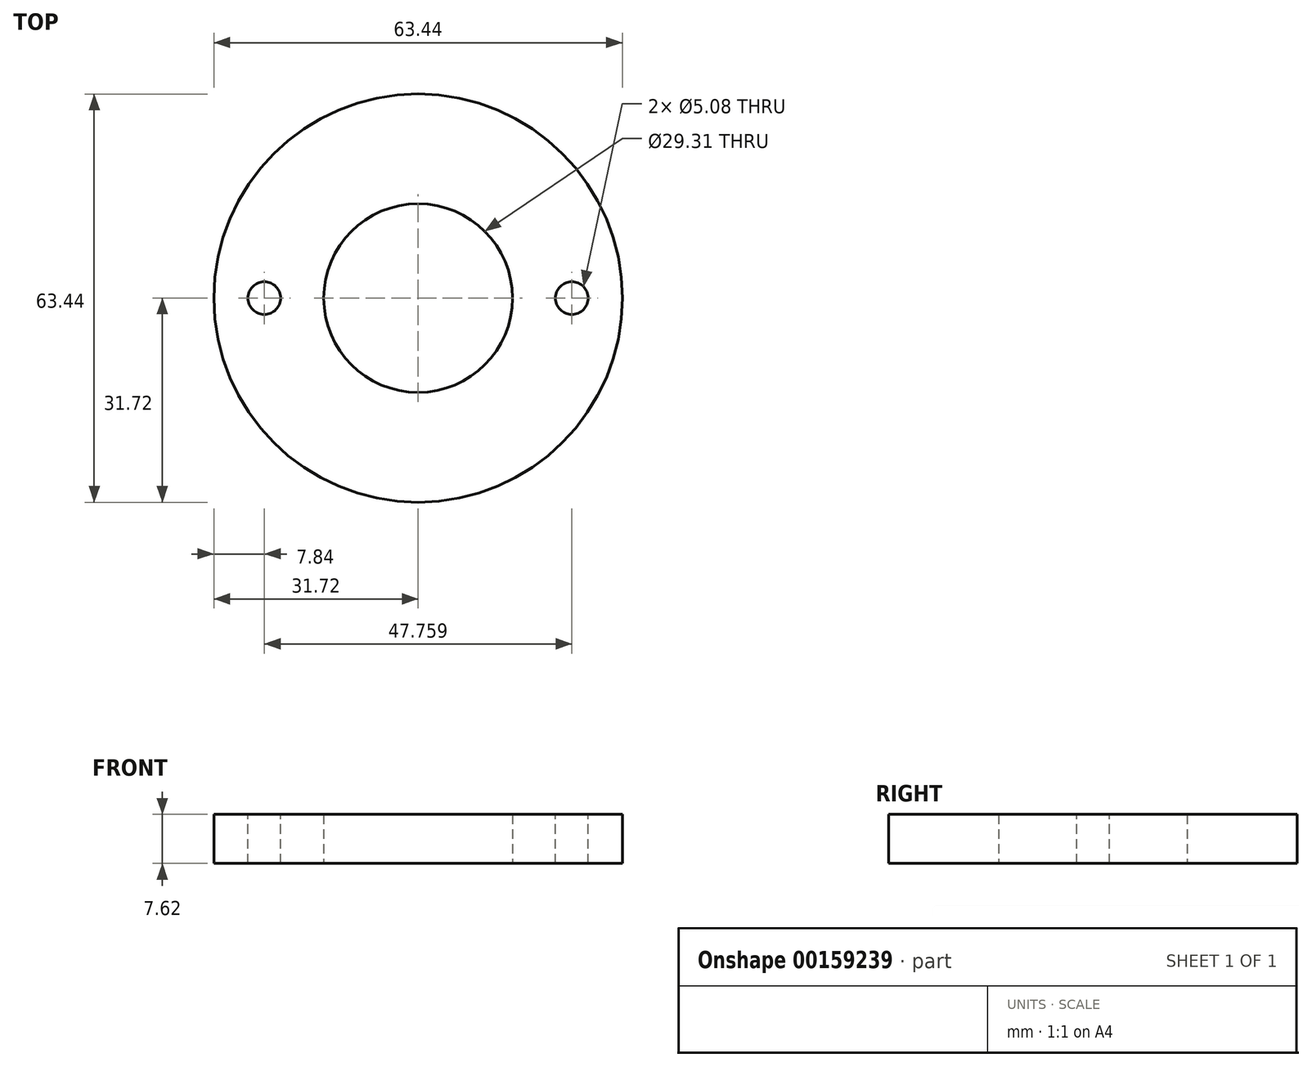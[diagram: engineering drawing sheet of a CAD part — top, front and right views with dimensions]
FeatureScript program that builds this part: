
annotation { "Feature Type Name" : "Feature", "Feature Type Description" : "" }
export const myFeature = defineFeature(function(context is Context, id is Id, definition is map)
    precondition{}
    {
        {
            var Q0;
            Q0=qCreatedBy(makeId("Top.planeOp"),FACE);
            var sketch = newSketch(context, id + "F0", { "sketchPlane" : qUnion([Q0])});
            skCircle(sketch, "E0", {"center": v(0, 0) * mm, "radius": 31.72 * mm});
            skCircle(sketch, "E1", {"center": v(0, 0) * mm, "radius": 14.66 * mm});
            skSolve(sketch);
        }
        {
            var Q0;
            Q0=makeQuery(id+"F0.imprint","IMPRINT",FACE,{"disambiguationData":[TD([[makeQuery(id+"F0.imprint","IMPRINT",EDGE,{"derivedFrom":sQuery(id+"F0.wireOp",EDGE,"E0")}),1.0]])]});
            extrude(context, id + "F1", {"entities" : qUnion([Q0]), "depth" : 7.62 * mm});
        }
        {
            var Q0;
            Q0=makeQuery(id+"F1.opExtrude","CAP_FACE",FACE,{"disambiguationData":[OSD([sQuery(id+"F0.wireOp",EDGE,"E0"),sQuery(id+"F0.wireOp",EDGE,"E1")])],"isStart":false});
            var sketch = newSketch(context, id + "F2", { "sketchPlane" : qUnion([Q0])});
            skCircle(sketch, "E2", {"center": v(-23.88, 0) * mm, "radius": 2.54 * mm});
            skCircle(sketch, "E3.MirrorC", {"center": v(23.88, 0) * mm, "radius": 2.54 * mm});
            skSolve(sketch);
        }
        {
            var Q0;
            Q0 = qSketchRegion(id + "F2", true);
            extrude(context, id + "F3", {"entities" : qUnion([Q0]), "operationType" : NewBodyOperationType.REMOVE, "oppositeDirection" : true, "depth" : 12.7 * mm});
        }
    });
